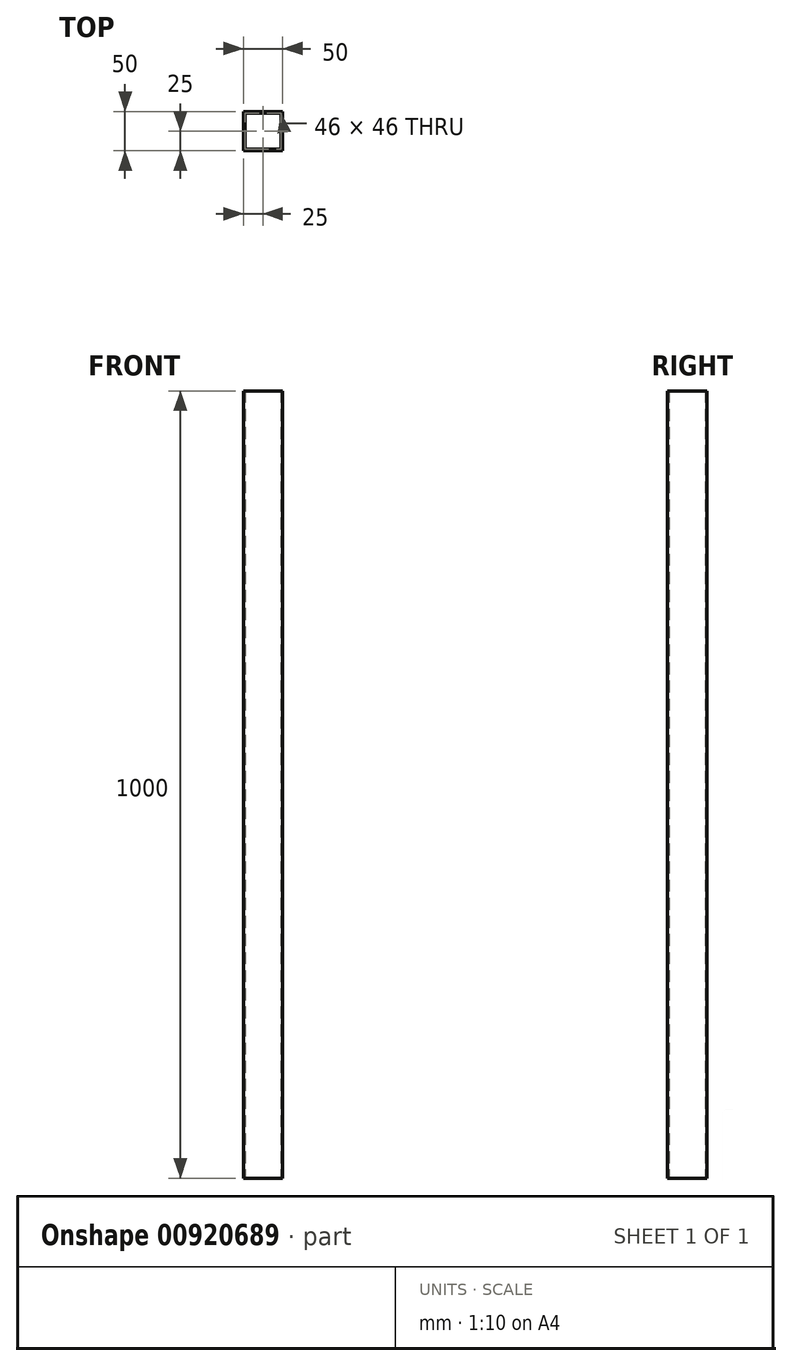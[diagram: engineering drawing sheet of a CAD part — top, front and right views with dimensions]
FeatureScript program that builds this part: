
annotation { "Feature Type Name" : "Feature", "Feature Type Description" : "" }
export const myFeature = defineFeature(function(context is Context, id is Id, definition is map)
    precondition{}
    {
        {
            var Q0;
            Q0=qCreatedBy(makeId("Top.planeOp"),FACE);
            var sketch = newSketch(context, id + "F0", { "sketchPlane" : qUnion([Q0])});
            skLineSegment(sketch, "E0.bottom", {"start": v(25, 25) * mm, "end": v(-25, 25) * mm});
            skLineSegment(sketch, "E0.top", {"start": v(25, -25) * mm, "end": v(-25, -25) * mm});
            skLineSegment(sketch, "E0.left", {"start": v(25, 25) * mm, "end": v(25, -25) * mm});
            skLineSegment(sketch, "E0.right", {"start": v(-25, 25) * mm, "end": v(-25, -25) * mm});
            skPoint(sketch, "E0.middle", {"position": v(0, 0) * mm});
            skLineSegment(sketch, "E1.0", {"start": v(23, 23) * mm, "end": v(-23, 23) * mm});
            skLineSegment(sketch, "E1.1", {"start": v(23, 23) * mm, "end": v(23, -23) * mm});
            skLineSegment(sketch, "E1.2", {"start": v(23, -23) * mm, "end": v(-23, -23) * mm});
            skLineSegment(sketch, "E1.3", {"start": v(-23, 23) * mm, "end": v(-23, -23) * mm});
            skSolve(sketch);
        }
        {
            var Q0;
            Q0=makeQuery(id+"F0.imprint","IMPRINT",FACE,{"disambiguationData":[TD([[makeQuery(id+"F0.imprint","IMPRINT",EDGE,{"derivedFrom":sQuery(id+"F0.wireOp",EDGE,"E0.bottom")}),1.0]])]});
            extrude(context, id + "F1", {"entities" : qUnion([Q0]), "depth" : 1000 * mm, "offsetDistance" : 25 * mm});
        }
    });
